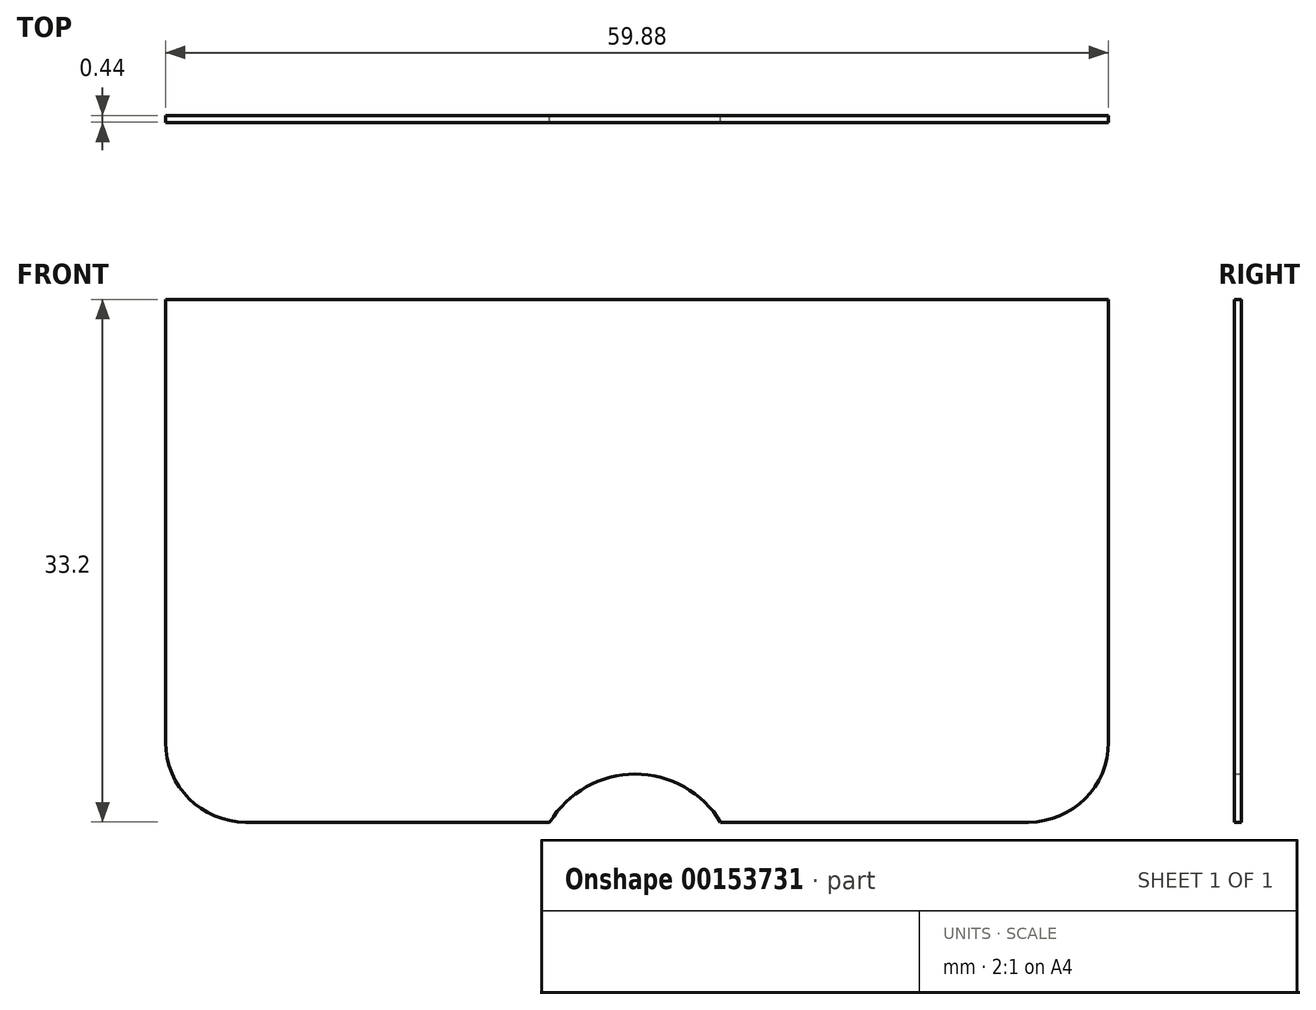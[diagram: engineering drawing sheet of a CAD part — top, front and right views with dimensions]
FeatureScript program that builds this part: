
annotation { "Feature Type Name" : "Feature", "Feature Type Description" : "" }
export const myFeature = defineFeature(function(context is Context, id is Id, definition is map)
    precondition{}
    {
        {
            var Q0;
            Q0=qCreatedBy(makeId("Front.planeOp"),FACE);
            var sketch = newSketch(context, id + "F0", { "sketchPlane" : qUnion([Q0])});
            skLineSegment(sketch, "E0", {"start": v(-29.89, 30.15) * mm, "end": v(-29.89, 2.03) * mm});
            skLineSegment(sketch, "E1", {"start": v(30, 30.15) * mm, "end": v(30, 2.03) * mm});
            skLineSegment(sketch, "E2", {"start": v(-29.89, 30.15) * mm, "end": v(30, 30.15) * mm});
            skLineSegment(sketch, "E3", {"start": v(-24.8, -3.05) * mm, "end": v(-5.5, -3.05) * mm});
            skPoint(sketch, "E4.visualSharp", {"position": v(-29.89, -3.05) * mm});
            skArc(sketch, "E4.filletArc", {"start": v(-29.89, 2.03) * mm, "mid": v(-28.4, -1.57) * mm, "end": v(-24.8, -3.05) * mm});
            skPoint(sketch, "E5.visualSharp", {"position": v(30, -3.05) * mm});
            skArc(sketch, "E5.filletArc", {"start": v(24.91, -3.05) * mm, "mid": v(28.5, -1.57) * mm, "end": v(30, 2.03) * mm});
            skArc(sketch, "E6", {"start": v(5.36, -3.05) * mm, "mid": v(-0.07, 0) * mm, "end": v(-5.5, -3.05) * mm});
            skLineSegment(sketch, "E7.trimOffspring", {"start": v(5.36, -3.05) * mm, "end": v(24.91, -3.05) * mm});
            skSolve(sketch);
        }
        {
            var Q0;
            Q0=makeQuery(id+"F0.imprint","IMPRINT",FACE,{"disambiguationData":[TD([[makeQuery(id+"F0.imprint","IMPRINT",EDGE,{"derivedFrom":sQuery(id+"F0.wireOp",EDGE,"E0")}),1.0]])]});
            extrude(context, id + "F1", {"entities" : qUnion([Q0]), "depth" : 0.44 * mm});
        }
    });
